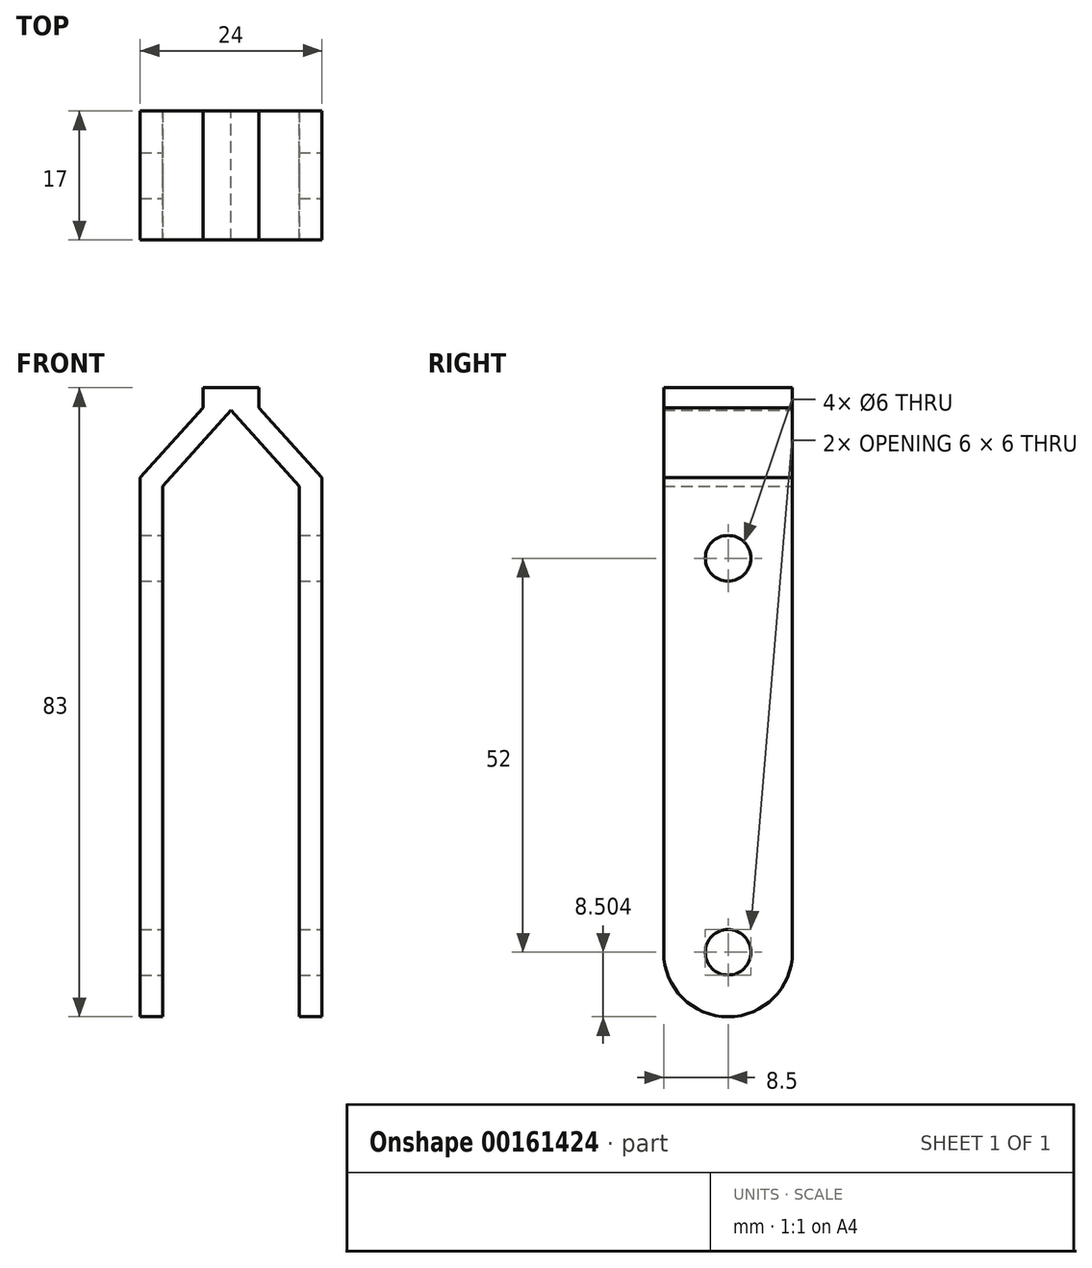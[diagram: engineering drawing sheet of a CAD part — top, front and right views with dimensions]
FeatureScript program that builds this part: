
annotation { "Feature Type Name" : "Feature", "Feature Type Description" : "" }
export const myFeature = defineFeature(function(context is Context, id is Id, definition is map)
    precondition{}
    {
        {
            var Q0;
            Q0=qCreatedBy(makeId("Front.planeOp"),FACE);
            var sketch = newSketch(context, id + "F0", { "sketchPlane" : qUnion([Q0])});
            skLineSegment(sketch, "E0.top", {"start": v(12, -74) * mm, "end": v(9, -74) * mm});
            skLineSegment(sketch, "E0.left", {"start": v(12, -2.84) * mm, "end": v(12, -74) * mm});
            skLineSegment(sketch, "E0.right", {"start": v(-12, -2.84) * mm, "end": v(-12, -74) * mm});
            skPoint(sketch, "E0.middle", {"position": v(0, 0) * mm});
            skLineSegment(sketch, "E1", {"start": v(-9, -74) * mm, "end": v(-9, -4) * mm});
            skLineSegment(sketch, "E2", {"start": v(9, -74) * mm, "end": v(9, -4) * mm});
            skLineSegment(sketch, "E3.trimOffspring", {"start": v(-9, -74) * mm, "end": v(-12, -74) * mm});
            skLineSegment(sketch, "E4.left", {"start": v(3.7, 9) * mm, "end": v(3.7, 6.38) * mm});
            skLineSegment(sketch, "E4.right", {"start": v(-3.7, 9) * mm, "end": v(-3.7, 6.38) * mm});
            skLineSegment(sketch, "E5", {"start": v(0, 6) * mm, "end": v(-9, -4) * mm});
            skLineSegment(sketch, "E6", {"start": v(0, 6) * mm, "end": v(9, -4) * mm});
            skLineSegment(sketch, "E7", {"start": v(-12, -2.84) * mm, "end": v(-3.7, 6.38) * mm});
            skLineSegment(sketch, "E8", {"start": v(3.7, 6.38) * mm, "end": v(12, -2.84) * mm});
            skPoint(sketch, "E9.orphan", {"position": v(-3.7, -86.57) * mm});
            skPoint(sketch, "E10.orphan", {"position": v(3.7, -86.57) * mm});
            skLineSegment(sketch, "E11.bottom", {"start": v(-3.7, 9) * mm, "end": v(3.7, 9) * mm});
            skSolve(sketch);
        }
        {
            var Q0;
            Q0 = qSketchRegion(id + "F0", true);
            extrude(context, id + "F1", {"entities" : qUnion([Q0]), "depth" : 25 * mm});
        }
        {
            var Q0;
            Q0=makeQuery(id+"F1.opExtrude","SWEPT_FACE",FACE,{"disambiguationData":[OSD([sQuery(id+"F0.wireOp",EDGE,"E0.left")])]});
            var sketch = newSketch(context, id + "F2", { "sketchPlane" : qUnion([Q0])});
            skLineSegment(sketch, "E12.bottom", {"start": v(-4, -74) * mm, "end": v(-21, -74) * mm});
            skLineSegment(sketch, "E12.left", {"start": v(-4, -74) * mm, "end": v(-4, 9) * mm});
            skLineSegment(sketch, "E12.right", {"start": v(-21, -74) * mm, "end": v(-21, 9) * mm});
            skPoint(sketch, "E12.middle", {"position": v(-12.5, -8.36) * mm});
            skPoint(sketch, "E12.middle.positionSnap0", {"position": v(-12.5, -2.84) * mm});
            skPoint(sketch, "E12.centerSnap0", {"position": v(-12.5, -2.84) * mm});
            skLineSegment(sketch, "E13", {"start": v(-4, 9) * mm, "end": v(-21, 9) * mm});
            skPoint(sketch, "E12.top.end.orphan", {"position": v(-21, 57.28) * mm});
            skPoint(sketch, "E14.orphan", {"position": v(-4, 57.28) * mm});
            skLineSegment(sketch, "E15.bottom", {"start": v(-27.98, 9) * mm, "end": v(3.39, 9) * mm});
            skLineSegment(sketch, "E15.top", {"start": v(-27.98, -74) * mm, "end": v(3.39, -74) * mm});
            skLineSegment(sketch, "E15.left", {"start": v(-27.98, 9) * mm, "end": v(-27.98, -74) * mm});
            skLineSegment(sketch, "E15.right", {"start": v(3.39, 9) * mm, "end": v(3.39, -74) * mm});
            skSolve(sketch);
        }
        {
            var Q0;
            {var subQ3=sQuery(id+"F0.wireOp",EDGE,"E0.left");var subQ6=makeQuery(id+"F1.opExtrude","CAP_EDGE",EDGE,{"disambiguationData":[OSD([subQ3])],"isStart":false});Q0=makeQuery(id+"F2.imprint","IMPRINT",FACE,{"disambiguationData":[TD([[makeQuery(id+"F2.imprint","IMPRINT",EDGE,{"derivedFrom":subQ6}),1.0]])]});}
            var Q1;
            {var subQ3=sQuery(id+"F0.wireOp",EDGE,"E0.left");var subQ6=makeQuery(id+"F1.opExtrude","CAP_EDGE",EDGE,{"disambiguationData":[OSD([subQ3])],"isStart":true});Q1=makeQuery(id+"F2.imprint","IMPRINT",FACE,{"disambiguationData":[TD([[makeQuery(id+"F2.imprint","IMPRINT",EDGE,{"derivedFrom":subQ6}),-1.0]])]});}
            var Q2;
            {var subQ0=sQuery(id+"F2.wireOp",EDGE,"E15.right");Q2=makeQuery(id+"F2.imprint","IMPRINT",FACE,{"disambiguationData":[TD([[makeQuery(id+"F2.imprint","IMPRINT",EDGE,{"derivedFrom":subQ0}),-1.0]])]});}
            var Q3;
            {var subQ0=sQuery(id+"F2.wireOp",EDGE,"E15.left");Q3=makeQuery(id+"F2.imprint","IMPRINT",FACE,{"disambiguationData":[TD([[makeQuery(id+"F2.imprint","IMPRINT",EDGE,{"derivedFrom":subQ0}),1.0]])]});}
            extrude(context, id + "F3", {"entities" : qUnion([Q0, Q1, Q2, Q3]), "operationType" : NewBodyOperationType.REMOVE, "oppositeDirection" : true, "depth" : 25 * mm});
        }
        {
            var Q0;
            Q0=makeQuery(id+"F1.opExtrude","SWEPT_FACE",FACE,{"disambiguationData":[OSD([sQuery(id+"F0.wireOp",EDGE,"E0.left")])]});
            var sketch = newSketch(context, id + "F4", { "sketchPlane" : qUnion([Q0])});
            skArc(sketch, "E16", {"start": v(-21, -65.5) * mm, "mid": v(-12.5, -74) * mm, "end": v(-4, -65.5) * mm});
            skPoint(sketch, "E16.centerSnap0", {"position": v(-12.5, -2.84) * mm});
            skPoint(sketch, "E17", {"position": v(-12.5, -13.5) * mm});
            skCircle(sketch, "E18", {"center": v(-12.5, -13.5) * mm, "radius": 3 * mm});
            skCircle(sketch, "E19", {"center": v(-12.5, -65.5) * mm, "radius": 3 * mm});
            skLineSegment(sketch, "E20.bottom", {"start": v(-21, -74) * mm, "end": v(-4, -74) * mm});
            skLineSegment(sketch, "E20.top", {"start": v(-21, -2.84) * mm, "end": v(-4, -2.84) * mm});
            skLineSegment(sketch, "E20.left", {"start": v(-21, -74) * mm, "end": v(-21, -2.84) * mm});
            skLineSegment(sketch, "E20.right", {"start": v(-4, -74) * mm, "end": v(-4, -2.84) * mm});
            skSolve(sketch);
        }
        {
            var Q0;
            {var subQ0=sQuery(id+"F4.wireOp",EDGE,"E20.left");var subQ1=sQuery(id+"F4.wireOp",EDGE,"E16");var subQ2=makeQuery(id+"F4.imprint","INTERSECT",VERTEX,{"derivedFrom":[subQ1,subQ0]});Q0=makeQuery(id+"F4.imprint","IMPRINT",FACE,{"disambiguationData":[TD([[makeQuery(id+"F4.imprint","IMPRINT",EDGE,{"disambiguationData":[TD([[subQ2,-1.0]])],"derivedFrom":subQ1}),-1.0]])]});}
            var Q1;
            {var subQ0=sQuery(id+"F4.wireOp",EDGE,"E20.right");var subQ1=sQuery(id+"F4.wireOp",EDGE,"E16");var subQ2=makeQuery(id+"F4.imprint","INTERSECT",VERTEX,{"derivedFrom":[subQ1,subQ0]});Q1=makeQuery(id+"F4.imprint","IMPRINT",FACE,{"disambiguationData":[TD([[makeQuery(id+"F4.imprint","IMPRINT",EDGE,{"disambiguationData":[TD([[subQ2,1.0]])],"derivedFrom":subQ1}),-1.0]])]});}
            var Q2;
            Q2=makeQuery(id+"F4.imprint","IMPRINT",FACE,{"disambiguationData":[TD([[makeQuery(id+"F4.imprint","IMPRINT",EDGE,{"derivedFrom":sQuery(id+"F4.wireOp",EDGE,"E19")}),1.0]])]});
            var Q3;
            Q3=makeQuery(id+"F4.imprint","IMPRINT",FACE,{"disambiguationData":[TD([[makeQuery(id+"F4.imprint","IMPRINT",EDGE,{"derivedFrom":sQuery(id+"F4.wireOp",EDGE,"E18")}),1.0]])]});
            extrude(context, id + "F5", {"entities" : qUnion([Q0, Q1, Q2, Q3]), "operationType" : NewBodyOperationType.REMOVE, "oppositeDirection" : true, "depth" : 25 * mm});
        }
    });
